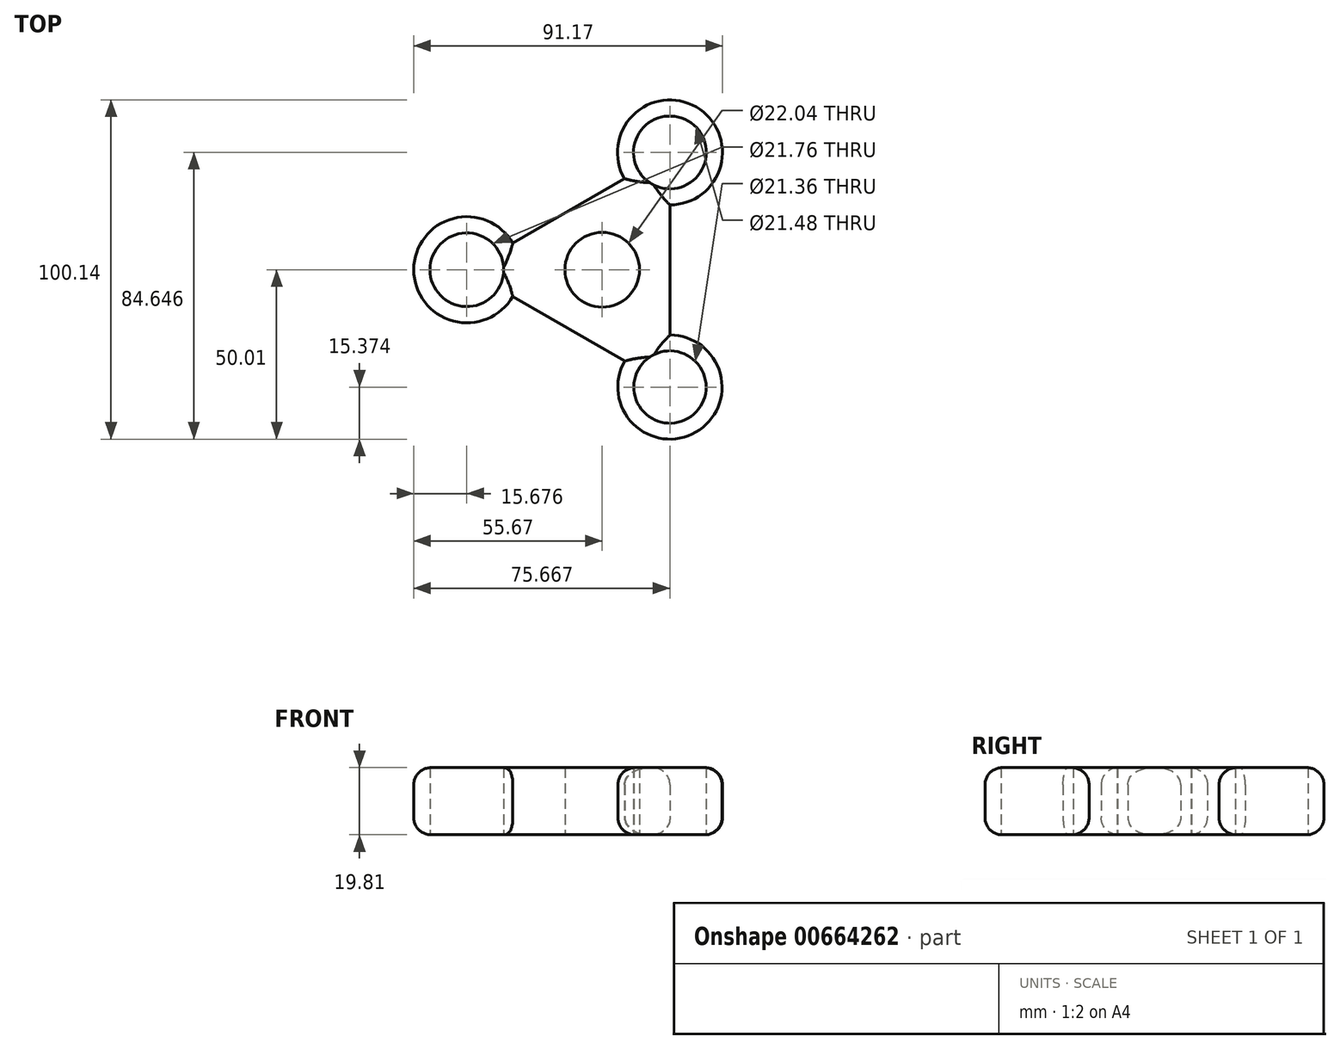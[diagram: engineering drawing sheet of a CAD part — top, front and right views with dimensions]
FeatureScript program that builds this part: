
annotation { "Feature Type Name" : "Feature", "Feature Type Description" : "" }
export const myFeature = defineFeature(function(context is Context, id is Id, definition is map)
    precondition{}
    {
        {
            var Q0;
            Q0=qCreatedBy(makeId("Top.planeOp"),FACE);
            var sketch = newSketch(context, id + "F0", { "sketchPlane" : qUnion([Q0])});
            skCircle(sketch, "E0.cCircle", {"center": v(0, 0) * mm, "radius": 20 * mm, "construction": true});
            skLineSegment(sketch, "E0.0", {"start": v(20, 34.64) * mm, "end": v(20, -34.64) * mm});
            skLineSegment(sketch, "E0.1", {"start": v(20, -34.64) * mm, "end": v(-40, 0) * mm});
            skLineSegment(sketch, "E0.2", {"start": v(-40, 0) * mm, "end": v(20, 34.64) * mm});
            skPoint(sketch, "E0.0.midPoint", {"position": v(20, 0) * mm});
            skCircle(sketch, "E1", {"center": v(20, 34.64) * mm, "radius": 15.5 * mm});
            skCircle(sketch, "E2", {"center": v(20, -34.64) * mm, "radius": 15.38 * mm});
            skCircle(sketch, "E3", {"center": v(-40, 0) * mm, "radius": 15.68 * mm});
            skSolve(sketch);
        }
        {
            var Q0;
            Q0 = qSketchRegion(id + "F0", true);
            extrude(context, id + "F1", {"entities" : qUnion([Q0]), "depth" : 19.8 * mm, "offsetDistance" : 25.4 * mm});
        }
        {
            var Q0;
            Q0=makeQuery(id+"F1.opExtrude","CAP_EDGE",EDGE,{"disambiguationData":[OSD([sQuery(id+"F0.wireOp",EDGE,"E0.0")])],"isStart":false});
            var Q1;
            Q1=makeQuery(id+"F1.opExtrude","CAP_EDGE",EDGE,{"disambiguationData":[OSD([sQuery(id+"F0.wireOp",EDGE,"E1")])],"isStart":false});
            var Q2;
            Q2=makeQuery(id+"F1.opExtrude","CAP_EDGE",EDGE,{"disambiguationData":[OSD([sQuery(id+"F0.wireOp",EDGE,"E0.2")])],"isStart":false});
            var Q3;
            Q3=makeQuery(id+"F1.opExtrude","CAP_EDGE",EDGE,{"disambiguationData":[OSD([sQuery(id+"F0.wireOp",EDGE,"E2")])],"isStart":false});
            var Q4;
            Q4=makeQuery(id+"F1.opExtrude","CAP_EDGE",EDGE,{"disambiguationData":[OSD([sQuery(id+"F0.wireOp",EDGE,"E0.1")])],"isStart":false});
            var Q5;
            Q5=makeQuery(id+"F1.opExtrude","CAP_EDGE",EDGE,{"disambiguationData":[OSD([sQuery(id+"F0.wireOp",EDGE,"E3")])],"isStart":false});
            var Q6;
            Q6=makeQuery(id+"F1.opExtrude","CAP_EDGE",EDGE,{"disambiguationData":[OSD([sQuery(id+"F0.wireOp",EDGE,"E2")])],"isStart":true});
            var Q7;
            Q7=makeQuery(id+"F1.opExtrude","CAP_EDGE",EDGE,{"disambiguationData":[OSD([sQuery(id+"F0.wireOp",EDGE,"E0.0")])],"isStart":true});
            var Q8;
            Q8=makeQuery(id+"F1.opExtrude","CAP_EDGE",EDGE,{"disambiguationData":[OSD([sQuery(id+"F0.wireOp",EDGE,"E1")])],"isStart":true});
            var Q9;
            Q9=makeQuery(id+"F1.opExtrude","CAP_EDGE",EDGE,{"disambiguationData":[OSD([sQuery(id+"F0.wireOp",EDGE,"E0.2")])],"isStart":true});
            var Q10;
            Q10=makeQuery(id+"F1.opExtrude","CAP_EDGE",EDGE,{"disambiguationData":[OSD([sQuery(id+"F0.wireOp",EDGE,"E3")])],"isStart":true});
            var Q11;
            Q11=makeQuery(id+"F1.opExtrude","CAP_EDGE",EDGE,{"disambiguationData":[OSD([sQuery(id+"F0.wireOp",EDGE,"E0.1")])],"isStart":true});
            fillet(context, id + "F2", {"entities" : qUnion([Q0, Q1, Q2, Q3, Q4, Q5, Q6, Q7, Q8, Q9, Q10, Q11]), "radius" : 5.08 * mm, "tangentPropagation" : true, "allowEdgeOverflow" : false});
        }
        {
            var Q0;
            Q0=makeQuery(id+"F1.opExtrude","CAP_FACE",FACE,{"disambiguationData":[OSD([sQuery(id+"F0.wireOp",EDGE,"E0.0"),sQuery(id+"F0.wireOp",EDGE,"E0.1"),sQuery(id+"F0.wireOp",EDGE,"E0.2"),sQuery(id+"F0.wireOp",EDGE,"E1"),sQuery(id+"F0.wireOp",EDGE,"E2"),sQuery(id+"F0.wireOp",EDGE,"E3")])],"isStart":true});
            var sketch = newSketch(context, id + "F3", { "sketchPlane" : qUnion([Q0])});
            skCircle(sketch, "E4", {"center": v(0, 0) * mm, "radius": 11.02 * mm});
            skSolve(sketch);
        }
        {
            var Q0;
            Q0=makeQuery(id+"F3.imprint","IMPRINT",FACE,{"disambiguationData":[TD([[makeQuery(id+"F3.imprint","IMPRINT",EDGE,{"derivedFrom":sQuery(id+"F3.wireOp",EDGE,"E4")}),1.0]])]});
            extrude(context, id + "F4", {"entities" : qUnion([Q0]), "operationType" : NewBodyOperationType.REMOVE, "oppositeDirection" : true, "depth" : 25.4 * mm, "offsetDistance" : 25.4 * mm});
        }
        {
            var Q0;
            Q0=makeQuery(id+"F1.opExtrude","CAP_FACE",FACE,{"disambiguationData":[OSD([sQuery(id+"F0.wireOp",EDGE,"E0.0"),sQuery(id+"F0.wireOp",EDGE,"E0.1"),sQuery(id+"F0.wireOp",EDGE,"E0.2"),sQuery(id+"F0.wireOp",EDGE,"E1"),sQuery(id+"F0.wireOp",EDGE,"E2"),sQuery(id+"F0.wireOp",EDGE,"E3")])],"isStart":true});
            var sketch = newSketch(context, id + "F5", { "sketchPlane" : qUnion([Q0])});
            skCircle(sketch, "E5", {"center": v(-40, 0) * mm, "radius": 10.88 * mm});
            skCircle(sketch, "E6", {"center": v(20, 34.64) * mm, "radius": 10.68 * mm});
            skCircle(sketch, "E7", {"center": v(20, -34.64) * mm, "radius": 10.74 * mm});
            skSolve(sketch);
        }
        {
            var Q0;
            Q0 = qSketchRegion(id + "F5", true);
            extrude(context, id + "F6", {"entities" : qUnion([Q0]), "operationType" : NewBodyOperationType.REMOVE, "oppositeDirection" : true, "depth" : 25.4 * mm, "offsetDistance" : 25.4 * mm});
        }
    });
